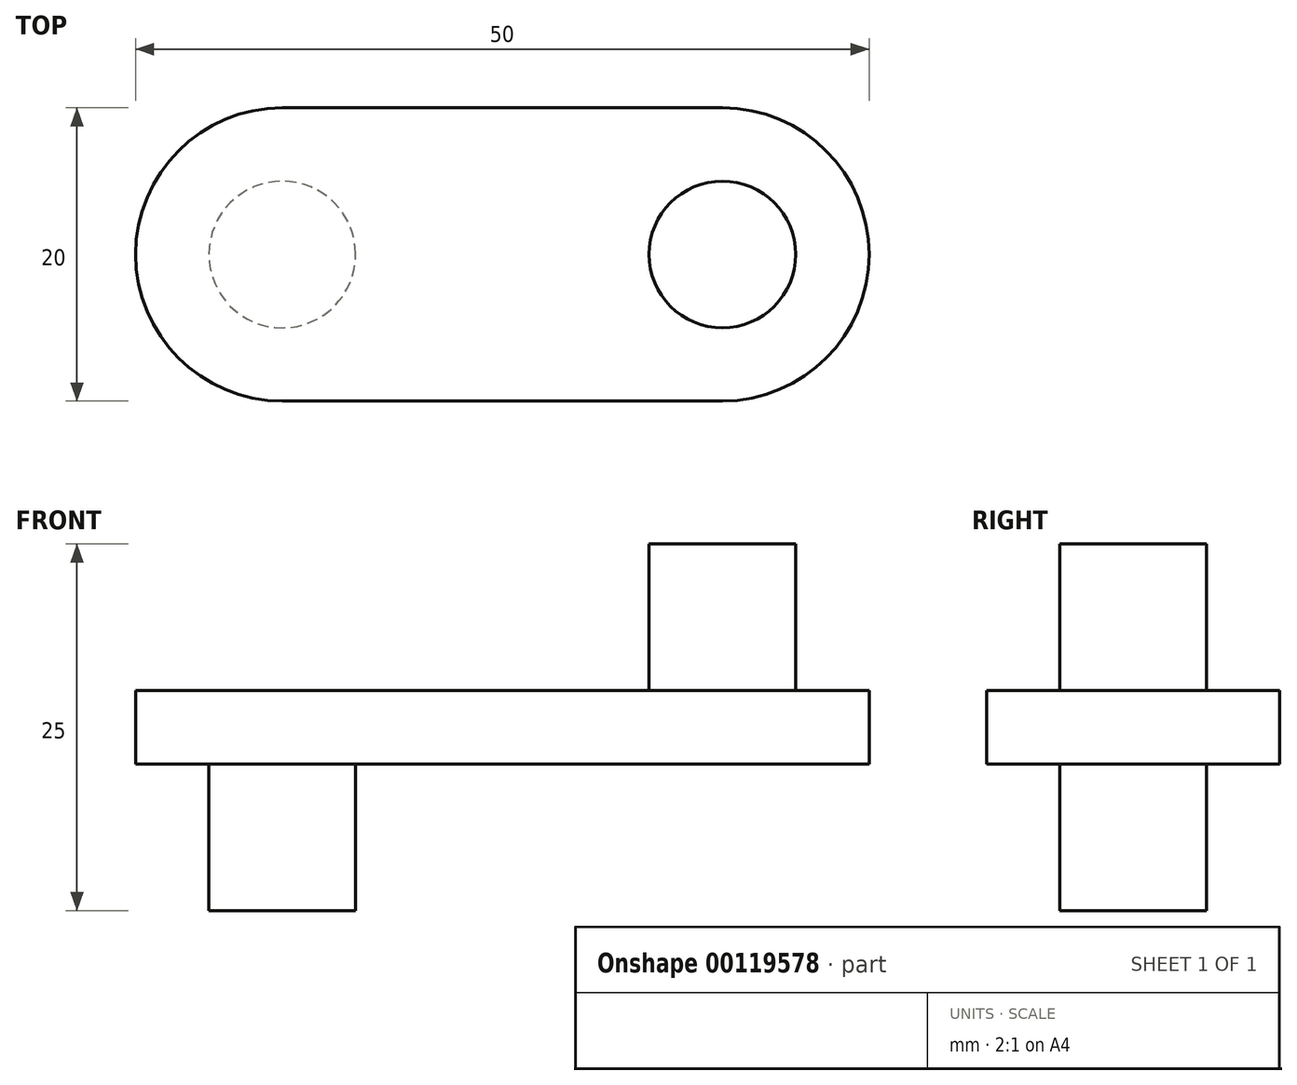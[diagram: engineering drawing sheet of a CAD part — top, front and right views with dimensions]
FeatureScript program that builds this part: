
annotation { "Feature Type Name" : "Feature", "Feature Type Description" : "" }
export const myFeature = defineFeature(function(context is Context, id is Id, definition is map)
    precondition{}
    {
        {
            var Q0;
            Q0=qCreatedBy(makeId("Top.planeOp"),FACE);
            var sketch = newSketch(context, id + "F0", { "sketchPlane" : qUnion([Q0])});
            skLineSegment(sketch, "E0", {"start": v(0, 0) * mm, "end": v(30, 0) * mm});
            skLineSegment(sketch, "E1", {"start": v(0, 20) * mm, "end": v(30, 20) * mm});
            skArc(sketch, "E2", {"start": v(0, 20) * mm, "mid": v(-10, 10) * mm, "end": v(0, 0) * mm});
            skArc(sketch, "E3", {"start": v(30, 20) * mm, "mid": v(40, 10) * mm, "end": v(30, 0) * mm});
            skSolve(sketch);
        }
        {
            var Q0;
            Q0 = qSketchRegion(id + "F0", true);
            extrude(context, id + "F1", {"entities" : qUnion([Q0]), "depth" : 5 * mm});
        }
        {
            var Q0;
            Q0=qCreatedBy(makeId("Top.planeOp"),FACE);
            var sketch = newSketch(context, id + "F2", { "sketchPlane" : qUnion([Q0])});
            skCircle(sketch, "E4", {"center": v(0, 10) * mm, "radius": 5 * mm});
            skSolve(sketch);
        }
        {
            var Q0;
            Q0 = qSketchRegion(id + "F2", true);
            extrude(context, id + "F3", {"entities" : qUnion([Q0]), "operationType" : NewBodyOperationType.ADD, "oppositeDirection" : true, "depth" : 10 * mm});
        }
        {
            var Q0;
            Q0=qCreatedBy(makeId("Top.planeOp"),FACE);
            var sketch = newSketch(context, id + "F4", { "sketchPlane" : qUnion([Q0])});
            skCircle(sketch, "E5", {"center": v(30, 10) * mm, "radius": 5 * mm});
            skSolve(sketch);
        }
        {
            var Q0;
            Q0 = qSketchRegion(id + "F4", true);
            extrude(context, id + "F5", {"entities" : qUnion([Q0]), "operationType" : NewBodyOperationType.ADD, "depth" : 15 * mm});
        }
    });
